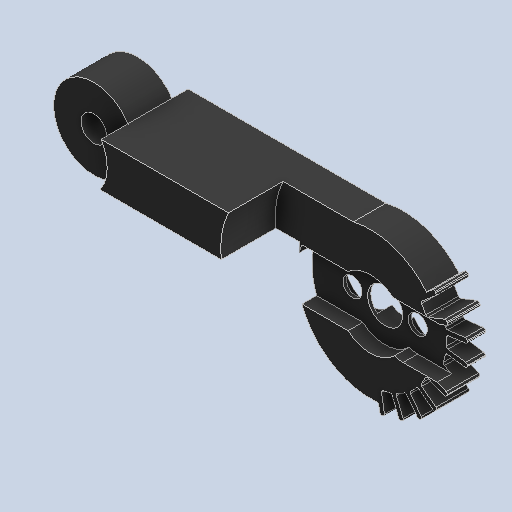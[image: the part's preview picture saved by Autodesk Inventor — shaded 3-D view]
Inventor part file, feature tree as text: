
AUTODESK INVENTOR PART (.ipt)
format: ipt  version: 2025.2 (Build 292293000, 293)  size: 292,352 bytes
history: native  units: mm
features: sketch x6, other x4
ambient origin geometry x8: Origin, YZ Plane, XZ Plane, XY Plane, X Axis, Y Axis, Z Axis, Center Point
bodies: Body1 (feature_tree)
feature tree (10):
  other  "Engrenagem1_0001_001.ipt"
  other  "Sólido1::Engrenagem1_0001_001.ipt"
  other  "OperaçãoIdentificador1"
  sketch  "Esboço1"  dims[d0=10.0mm]
  sketch  "Esboço2"
  sketch  "Esboço5"
  sketch  "Esboço6"
  sketch  "Esboço7"
  sketch  "Esboço8"
  other  "Sólido1"
